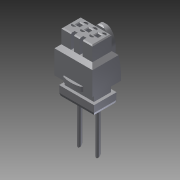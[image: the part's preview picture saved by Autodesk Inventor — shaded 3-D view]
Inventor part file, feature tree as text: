
AUTODESK INVENTOR PART (.ipt)
format: ipt  version: 2014 (Build 180170000, 170)  size: 326,656 bytes
history: native  units: mm
features: extrude x22, sketch x22, other x7
ambient origin geometry x8: Origin, YZ Plane, XZ Plane, XY Plane, X Axis, Y Axis, Z Axis, Center Point
bodies: Solid1 (feature_tree)
feature tree (51):
  extrude  "Extrusion1"  Depth=12.0mm TaperAngle=0.0deg
  extrude  "Extrusion2"  Depth=4.0mm TaperAngle=0.0deg
  extrude  "Extrusion3"  Depth=1.0mm TaperAngle=0.0deg
  extrude  "Extrusion4"  Depth=3.2mm TaperAngle=0.0deg
  extrude  "Extrusion5"  Depth=2.9mm TaperAngle=0.0deg
  extrude  "Extrusion6"  Depth=2.9mm TaperAngle=0.0deg
  extrude  "Extrusion7"  Depth=2.9mm TaperAngle=0.0deg
  extrude  "Extrusion8"  Depth=2.9mm TaperAngle=0.0deg
  extrude  "Extrusion9"  Depth=2.9mm TaperAngle=0.0deg
  extrude  "Extrusion10"  Depth=10.0mm TaperAngle=0.0deg
  extrude  "Extrusion11"  Depth=5.0mm TaperAngle=0.0deg
  extrude  "Extrusion12"  [1 undecoded]
  extrude  "Extrusion13"  [1 undecoded]
  extrude  "Extrusion14"  [1 undecoded]
  extrude  "Extrusion15"  [1 undecoded]
  extrude  "Extrusion16"  [1 undecoded]
  extrude  "Extrusion17"  [1 undecoded]
  extrude  "Extrusion18"  [1 undecoded]
  extrude  "Extrusion19"  [1 undecoded]
  extrude  "Extrusion20"  [1 undecoded]
  extrude  "Extrusion21"  [1 undecoded]
  extrude  "Extrusion22"  [1 undecoded]
  other  "NEBV_XY"
  other  "NEBV_YZ"
  other  "NEBV_ZX"
  other  "NEBV_X"
  other  "NEBV_Y"
  other  "NEBV_Z"
  other  "NEBV_Center"
  sketch  "Sketch_9"  dims[d32=2.9mm d33=0.0mm d34=1.1mm d35=0.0mm]
  sketch  "Sketch_23"
  sketch  "Sketch_1"  dims[d0=8.3mm d1=0.0mm d2=12.0mm d3=0.0mm]
  sketch  "Sketch_2"  dims[d4=2.0mm d5=0.0mm d6=4.0mm d7=0.0mm]
  sketch  "Sketch_3"  dims[d8=3.0mm d9=0.0mm d10=1.0mm d11=0.0mm]
  sketch  "Sketch_4"  dims[d12=1.0mm d13=0.0mm d14=3.2mm d15=0.0mm]
  sketch  "Sketch_5"  dims[d16=2.9mm d17=0.0mm d18=2.9mm d19=0.0mm]
  sketch  "Sketch_6"  dims[d20=2.9mm d21=0.0mm d22=2.9mm d23=0.0mm]
  sketch  "Sketch_19"
  sketch  "Sketch_20"
  sketch  "Sketch_21"
  sketch  "Sketch_7"  dims[d24=2.9mm d25=0.0mm d26=2.9mm d27=0.0mm]
  sketch  "Sketch_8"  dims[d28=2.9mm d29=0.0mm d30=2.9mm d31=0.0mm]
  sketch  "Sketch_10"  dims[d36=6.0mm d37=0.0mm d38=10.0mm d39=0.0mm]
  sketch  "Sketch_11"  dims[d40=10.0mm d41=0.0mm d42=5.0mm d43=0.0mm]
  sketch  "Sketch_12"
  sketch  "Sketch_13"
  sketch  "Sketch_14"
  sketch  "Sketch_15"
  sketch  "Sketch_16"
  sketch  "Sketch_17"
  sketch  "Sketch_18"
note: 11 required parameter values undecoded (feature->parameter linkage not recoverable at this tier; creation-order binding heuristic only, values carry confidence <= 0.55)
